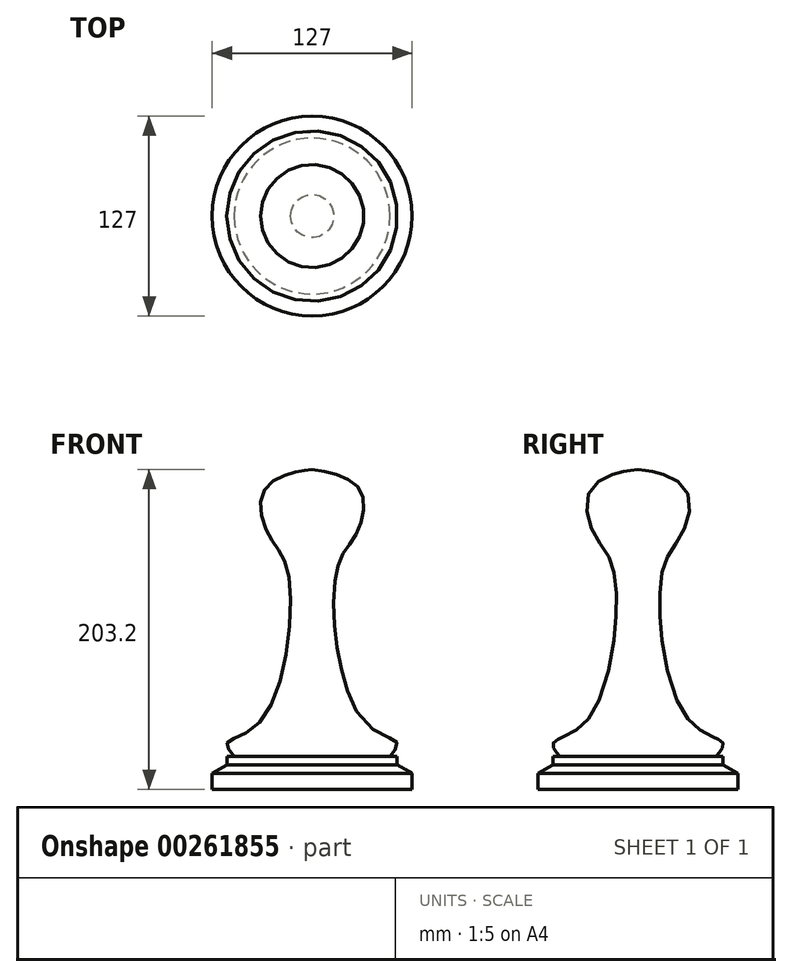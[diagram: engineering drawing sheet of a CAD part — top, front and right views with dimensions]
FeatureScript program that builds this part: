
annotation { "Feature Type Name" : "Feature", "Feature Type Description" : "" }
export const myFeature = defineFeature(function(context is Context, id is Id, definition is map)
    precondition{}
    {
        {
            var Q0;
            Q0=qCreatedBy(makeId("Front.planeOp"),FACE);
            var sketch = newSketch(context, id + "F0", { "sketchPlane" : qUnion([Q0])});
            skLineSegment(sketch, "E0", {"start": v(0, 112.86) * mm, "end": v(0, -113.8) * mm, "construction": true});
            skLineSegment(sketch, "E1", {"start": v(0, 101.37) * mm, "end": v(0, -101.83) * mm});
            skLineSegment(sketch, "E2", {"start": v(0, -101.83) * mm, "end": v(-63.5, -101.83) * mm});
            skLineSegment(sketch, "E3", {"start": v(-63.5, -101.83) * mm, "end": v(-63.5, -91.52) * mm});
            skLineSegment(sketch, "E4", {"start": v(-63.5, -91.52) * mm, "end": v(-54.02, -86.12) * mm});
            skLineSegment(sketch, "E5", {"start": v(-54.02, -86.12) * mm, "end": v(-54.02, -80.76) * mm});
            skLineSegment(sketch, "E6", {"start": v(-54.02, -80.76) * mm, "end": v(-49.52, -80.76) * mm});
            skFitSpline(sketch, "E7", {"points": [v(-49.52, -80.76) * mm, v(-54.02, -72.54) * mm, v(-32.33, -58) * mm, v(-15.5, 36.8) * mm, v(-27.55, 59.8) * mm, v(-30.98, 87.37) * mm, v(-11.69, 99.4) * mm, v(0, 101.37) * mm], "startDerivative": vector(-97.02, 109.29) * mm, "endDerivative": vector(110.05, 11.65) * mm});
            skSolve(sketch);
        }
        {
            var Q0;
            Q0=makeQuery(id+"F0.imprint","IMPRINT",FACE,{"disambiguationData":[TD([[makeQuery(id+"F0.imprint","IMPRINT",EDGE,{"derivedFrom":sQuery(id+"F0.wireOp",EDGE,"E1")}),-1.0]])]});
            var Q1;
            Q1=sQuery(id+"F0.wireOp",EDGE,"E0");
            revolve(context, id + "F1", {"entities" : qUnion([Q0]), "axis" : qUnion([Q1]), "revolveType" : RevolveType.FULL});
        }
    });
